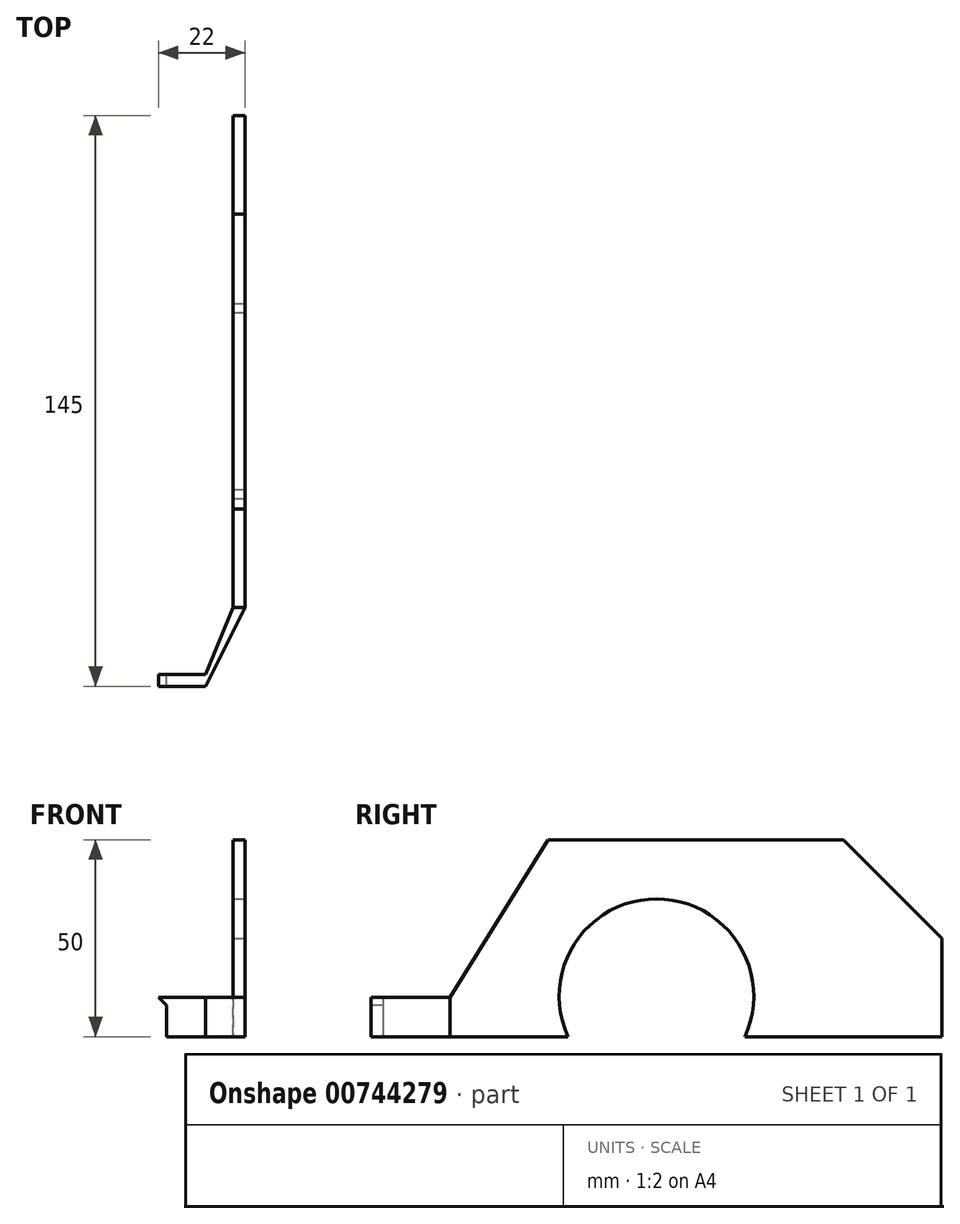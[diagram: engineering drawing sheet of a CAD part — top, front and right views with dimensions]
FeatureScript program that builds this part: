
annotation { "Feature Type Name" : "Feature", "Feature Type Description" : "" }
export const myFeature = defineFeature(function(context is Context, id is Id, definition is map)
    precondition{}
    {
        {
            var Q0;
            Q0=qCreatedBy(makeId("Top.planeOp"),FACE);
            var sketch = newSketch(context, id + "F0", { "sketchPlane" : qUnion([Q0])});
            skLineSegment(sketch, "E0", {"start": v(0, 0) * mm, "end": v(0, 3) * mm});
            skLineSegment(sketch, "E1", {"start": v(0, 3) * mm, "end": v(10, 3) * mm});
            skLineSegment(sketch, "E2", {"start": v(10, 3) * mm, "end": v(17, 20) * mm});
            skLineSegment(sketch, "E3", {"start": v(17, 20) * mm, "end": v(17, 145) * mm});
            skLineSegment(sketch, "E4", {"start": v(17, 145) * mm, "end": v(20, 145) * mm});
            skLineSegment(sketch, "E5", {"start": v(20, 145) * mm, "end": v(20, 20) * mm});
            skLineSegment(sketch, "E6", {"start": v(20, 20) * mm, "end": v(10, 0) * mm});
            skLineSegment(sketch, "E7", {"start": v(10, 0) * mm, "end": v(0, 0) * mm});
            skSolve(sketch);
        }
        {
            var Q0;
            Q0=makeQuery(id+"F0.imprint","IMPRINT",FACE,{"disambiguationData":[TD([[makeQuery(id+"F0.imprint","IMPRINT",EDGE,{"derivedFrom":sQuery(id+"F0.wireOp",EDGE,"E0")}),-1.0]])]});
            extrude(context, id + "F1", {"entities" : qUnion([Q0]), "depth" : 10 * mm, "offsetDistance" : 25 * mm});
        }
        {
            var Q0;
            Q0=qCreatedBy(makeId("Front.planeOp"),FACE);
            var sketch = newSketch(context, id + "F2", { "sketchPlane" : qUnion([Q0])});
            skLineSegment(sketch, "E8", {"start": v(0, 10) * mm, "end": v(-2, 10) * mm});
            skLineSegment(sketch, "E9", {"start": v(-2, 10) * mm, "end": v(0, 8) * mm});
            skLineSegment(sketch, "E10", {"start": v(0, 8) * mm, "end": v(0, 10) * mm});
            skSolve(sketch);
        }
        {
            var Q0;
            Q0 = qSketchRegion(id + "F2", true);
            extrude(context, id + "F3", {"entities" : qUnion([Q0]), "operationType" : NewBodyOperationType.ADD, "oppositeDirection" : true, "depth" : 3 * mm, "offsetDistance" : 25 * mm});
        }
        {
            var Q0;
            Q0=makeQuery(id+"F3.boolean.opBoolean","MERGE",FACE,{"derivedFrom":[makeQuery(id+"F1.opExtrude","CAP_FACE",FACE,{"disambiguationData":[OSD([sQuery(id+"F0.wireOp",EDGE,"E0"),sQuery(id+"F0.wireOp",EDGE,"E1"),sQuery(id+"F0.wireOp",EDGE,"E2"),sQuery(id+"F0.wireOp",EDGE,"E3"),sQuery(id+"F0.wireOp",EDGE,"E4"),sQuery(id+"F0.wireOp",EDGE,"E5"),sQuery(id+"F0.wireOp",EDGE,"E6"),sQuery(id+"F0.wireOp",EDGE,"E7")])],"isStart":false}),makeQuery(id+"F3.opExtrude","SWEPT_FACE",FACE,{"disambiguationData":[OSD([sQuery(id+"F2.wireOp",EDGE,"E8")])]})]});
            var sketch = newSketch(context, id + "F4", { "sketchPlane" : qUnion([Q0])});
            skLineSegment(sketch, "E11.bottom", {"start": v(20, 20) * mm, "end": v(17, 20) * mm});
            skLineSegment(sketch, "E11.top", {"start": v(20, 145) * mm, "end": v(17, 145) * mm});
            skLineSegment(sketch, "E11.left", {"start": v(20, 20) * mm, "end": v(20, 145) * mm});
            skLineSegment(sketch, "E11.right", {"start": v(17, 20) * mm, "end": v(17, 145) * mm});
            skSolve(sketch);
        }
        {
            var Q0;
            Q0 = qSketchRegion(id + "F4", true);
            extrude(context, id + "F5", {"entities" : qUnion([Q0]), "operationType" : NewBodyOperationType.ADD, "depth" : 40 * mm, "offsetDistance" : 25 * mm});
        }
        {
            var Q0;
            Q0=makeQuery(id+"F5.opExtrude","CAP_EDGE",EDGE,{"disambiguationData":[OSD([sQuery(id+"F4.wireOp",EDGE,"E11.bottom")])],"isStart":false});
            chamfer(context, id + "F6", {"entities" : qUnion([Q0]), "chamferType" : ChamferType.TWO_OFFSETS, "width1" : 40 * mm, "oppositeDirection" : false, "width2" : 25 * mm, "tangentPropagation" : true});
        }
        {
            var Q0;
            Q0=makeQuery(id+"F5.opExtrude","CAP_EDGE",EDGE,{"disambiguationData":[OSD([sQuery(id+"F4.wireOp",EDGE,"E11.top")])],"isStart":false});
            chamfer(context, id + "F7", {"entities" : qUnion([Q0]), "width" : 25 * mm, "tangentPropagation" : true});
        }
        {
            var Q0;
            Q0=makeQuery(id+"F5.boolean.opBoolean","MERGE",FACE,{"derivedFrom":[makeQuery(id+"F1.opExtrude","SWEPT_FACE",FACE,{"disambiguationData":[OSD([sQuery(id+"F0.wireOp",EDGE,"E5")])]}),makeQuery(id+"F5.opExtrude","SWEPT_FACE",FACE,{"disambiguationData":[OSD([sQuery(id+"F4.wireOp",EDGE,"E11.left")])]})]});
            var sketch = newSketch(context, id + "F8", { "sketchPlane" : qUnion([Q0])});
            skArc(sketch, "E12", {"start": v(95, 0) * mm, "mid": v(72.5, 35) * mm, "end": v(50, 0) * mm});
            skSolve(sketch);
        }
        {
            var Q0;
            {var subQ0=sQuery(id+"F8.wireOp",EDGE,"E12");Q0=makeQuery(id+"F8.imprint","IMPRINT",FACE,{"disambiguationData":[TD([[makeQuery(id+"F8.imprint","IMPRINT",EDGE,{"derivedFrom":subQ0}),1.0]])]});}
            extrude(context, id + "F9", {"entities" : qUnion([Q0]), "operationType" : NewBodyOperationType.REMOVE, "oppositeDirection" : true, "depth" : 25 * mm, "offsetDistance" : 25 * mm});
        }
    });
